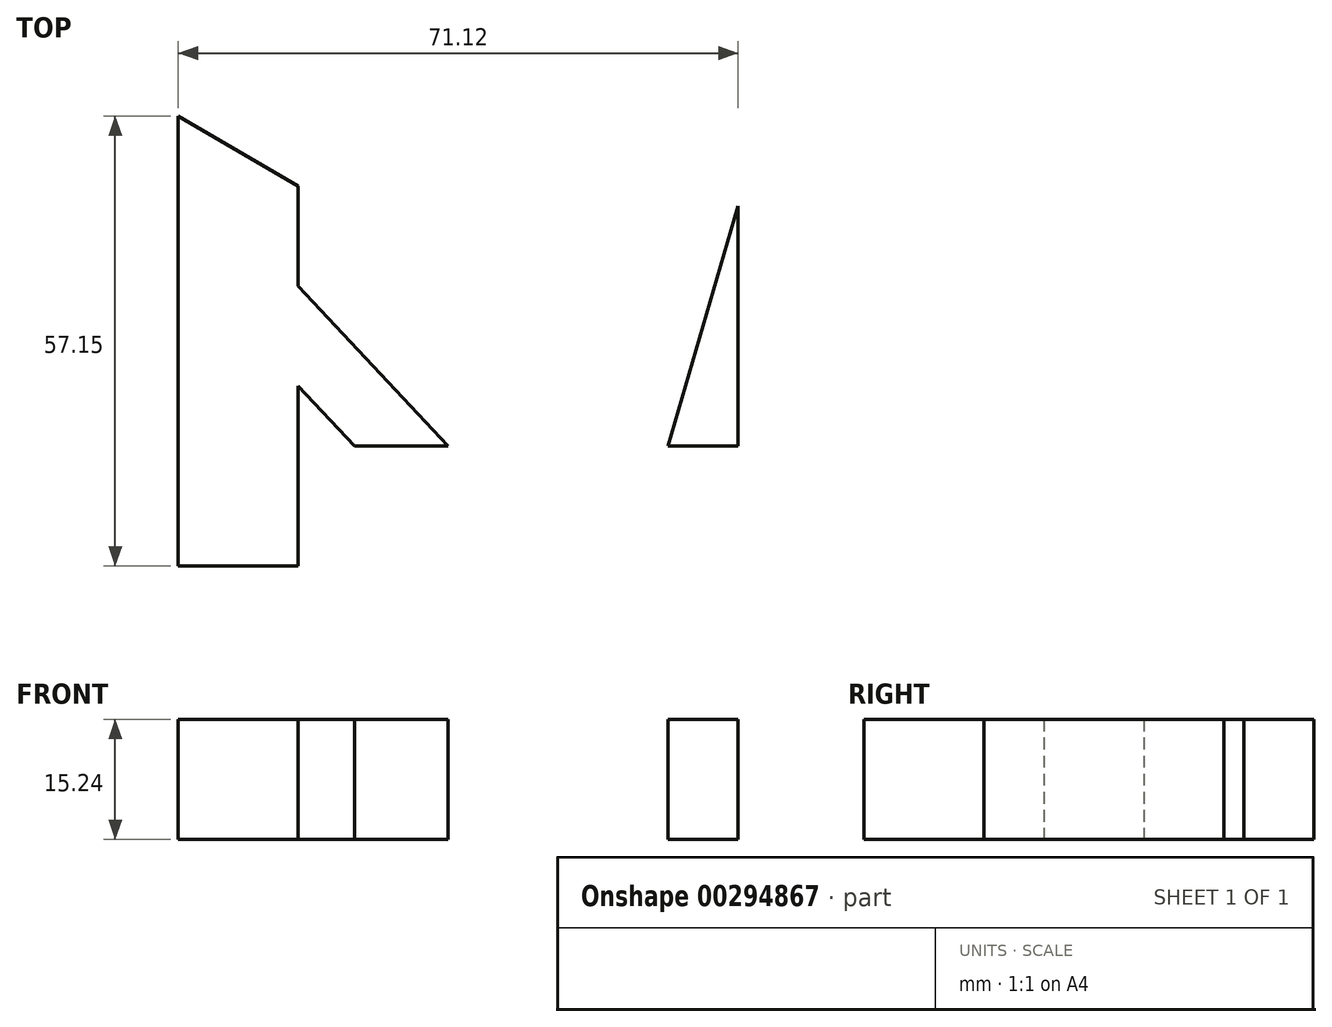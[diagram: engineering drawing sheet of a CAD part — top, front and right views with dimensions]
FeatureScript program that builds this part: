
annotation { "Feature Type Name" : "Feature", "Feature Type Description" : "" }
export const myFeature = defineFeature(function(context is Context, id is Id, definition is map)
    precondition{}
    {
        {
            var Q0;
            Q0=qCreatedBy(makeId("Top.planeOp"),FACE);
            var sketch = newSketch(context, id + "F0", { "sketchPlane" : qUnion([Q0])});
            skLineSegment(sketch, "E0.bottom", {"start": v(0, 57.15) * mm, "end": v(15.24, 57.15) * mm});
            skLineSegment(sketch, "E0.top", {"start": v(0, 0) * mm, "end": v(15.24, 0) * mm});
            skLineSegment(sketch, "E0.left", {"start": v(0, 57.15) * mm, "end": v(0, 0) * mm});
            skLineSegment(sketch, "E0.right", {"start": v(15.24, 57.15) * mm, "end": v(15.24, 0) * mm});
            skLineSegment(sketch, "E1.top", {"start": v(15.24, 15.24) * mm, "end": v(78.74, 15.24) * mm});
            skLineSegment(sketch, "E1.left", {"start": v(15.24, 0) * mm, "end": v(15.24, 15.24) * mm});
            skLineSegment(sketch, "E1.right", {"start": v(78.74, 7.62) * mm, "end": v(78.74, 15.24) * mm});
            skLineSegment(sketch, "E2.bottom", {"start": v(78.74, 15.24) * mm, "end": v(71.12, 15.24) * mm});
            skLineSegment(sketch, "E2.top", {"start": v(78.74, 45.72) * mm, "end": v(71.12, 45.72) * mm});
            skLineSegment(sketch, "E2.left", {"start": v(78.74, 15.24) * mm, "end": v(78.74, 45.72) * mm});
            skLineSegment(sketch, "E2.right", {"start": v(71.12, 15.24) * mm, "end": v(71.12, 45.72) * mm});
            skLineSegment(sketch, "E3", {"start": v(71.12, 45.72) * mm, "end": v(62.23, 15.24) * mm});
            skLineSegment(sketch, "E4", {"start": v(15.24, 35.56) * mm, "end": v(34.3, 15.24) * mm});
            skLineSegment(sketch, "E5", {"start": v(15.24, 22.86) * mm, "end": v(22.38, 15.24) * mm});
            skLineSegment(sketch, "E6", {"start": v(0, 57.15) * mm, "end": v(15.24, 48.26) * mm});
            skLineSegment(sketch, "E7", {"start": v(15.24, 0) * mm, "end": v(78.74, 7.62) * mm});
            skSolve(sketch);
        }
        {
            var Q0;
            Q0=makeQuery(id+"F0.imprint","IMPRINT",FACE,{"disambiguationData":[TD([[makeQuery(id+"F0.imprint","IMPRINT",EDGE,{"derivedFrom":sQuery(id+"F0.wireOp",EDGE,"E0.top")}),1.0]])]});
            var Q1;
            {var subQ0=sQuery(id+"F0.wireOp",EDGE,"E4");Q1=makeQuery(id+"F0.imprint","IMPRINT",FACE,{"disambiguationData":[TD([[makeQuery(id+"F0.imprint","IMPRINT",EDGE,{"derivedFrom":subQ0}),-1.0]])]});}
            var Q2;
            {var subQ5=sQuery(id+"F0.wireOp",EDGE,"E1.left");Q2=makeQuery(id+"F0.imprint","IMPRINT",FACE,{"disambiguationData":[TD([[makeQuery(id+"F0.imprint","IMPRINT",EDGE,{"derivedFrom":subQ5}),-1.0]])]});}
            var Q3;
            {var subQ0=sQuery(id+"F0.wireOp",EDGE,"E2.right");Q3=makeQuery(id+"F0.imprint","IMPRINT",FACE,{"disambiguationData":[TD([[makeQuery(id+"F0.imprint","IMPRINT",EDGE,{"derivedFrom":subQ0}),1.0]])]});}
            var Q4;
            Q4=makeQuery(id+"F0.imprint","IMPRINT",FACE,{"disambiguationData":[TD([[makeQuery(id+"F0.imprint","IMPRINT",EDGE,{"derivedFrom":sQuery(id+"F0.wireOp",EDGE,"E2.bottom")}),-1.0]])]});
            extrude(context, id + "F1", {"entities" : qUnion([Q0, Q1, Q2, Q3, Q4]), "depth" : 15.24 * mm});
        }
    });
